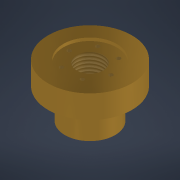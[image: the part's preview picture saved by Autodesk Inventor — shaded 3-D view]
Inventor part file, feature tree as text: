
AUTODESK INVENTOR PART (.ipt)
format: ipt  version: 2022 (Build 260153000, 153)  size: 130,048 bytes
history: native  units: mm
features: extrude x4, sketch x4, projected_geometry x3, thread x1, plane x1
ambient origin geometry x8: Origin, YZ Plane, XZ Plane, XY Plane, X Axis, Y Axis, Z Axis, Center Point
bodies: Solid1 (feature_tree)
feature tree (13):
  extrude  "Extrusion1"  Depth=30.0mm
  thread  "Thread1"  [1 undecoded]
  extrude  "Extrusion2"  Depth=20.0mm
  extrude  "Extrusion3"  Depth=30.0mm
  sketch  "Sketch6"  dims[d13=3.0mm d14=0.0mm d15=47.0mm d27=40.0mm d28=10.0mm d29=0.0mm d12=0.872665mm]
  plane  "Work Plane1"
  extrude  "Extrusion4"  Depth=10.0mm
  sketch  "Sketch1"  dims[d0=16.0mm d1=30.0mm d2=30.0mm d3=0.0mm]
  sketch  "Sketch2"  dims[d4=20.0mm d5=0.0mm d6=90.0mm]
  projected_geometry  "Projected Loop1"
  sketch  "Sketch4"  dims[d7=12.0mm d8=0.0mm d11=30.0mm]
  projected_geometry  "Projected Loop3"
  projected_geometry  "Projected Loop4"
note: 1 required parameter value undecoded (feature->parameter linkage not recoverable at this tier; creation-order binding heuristic only, values carry confidence <= 0.55)
